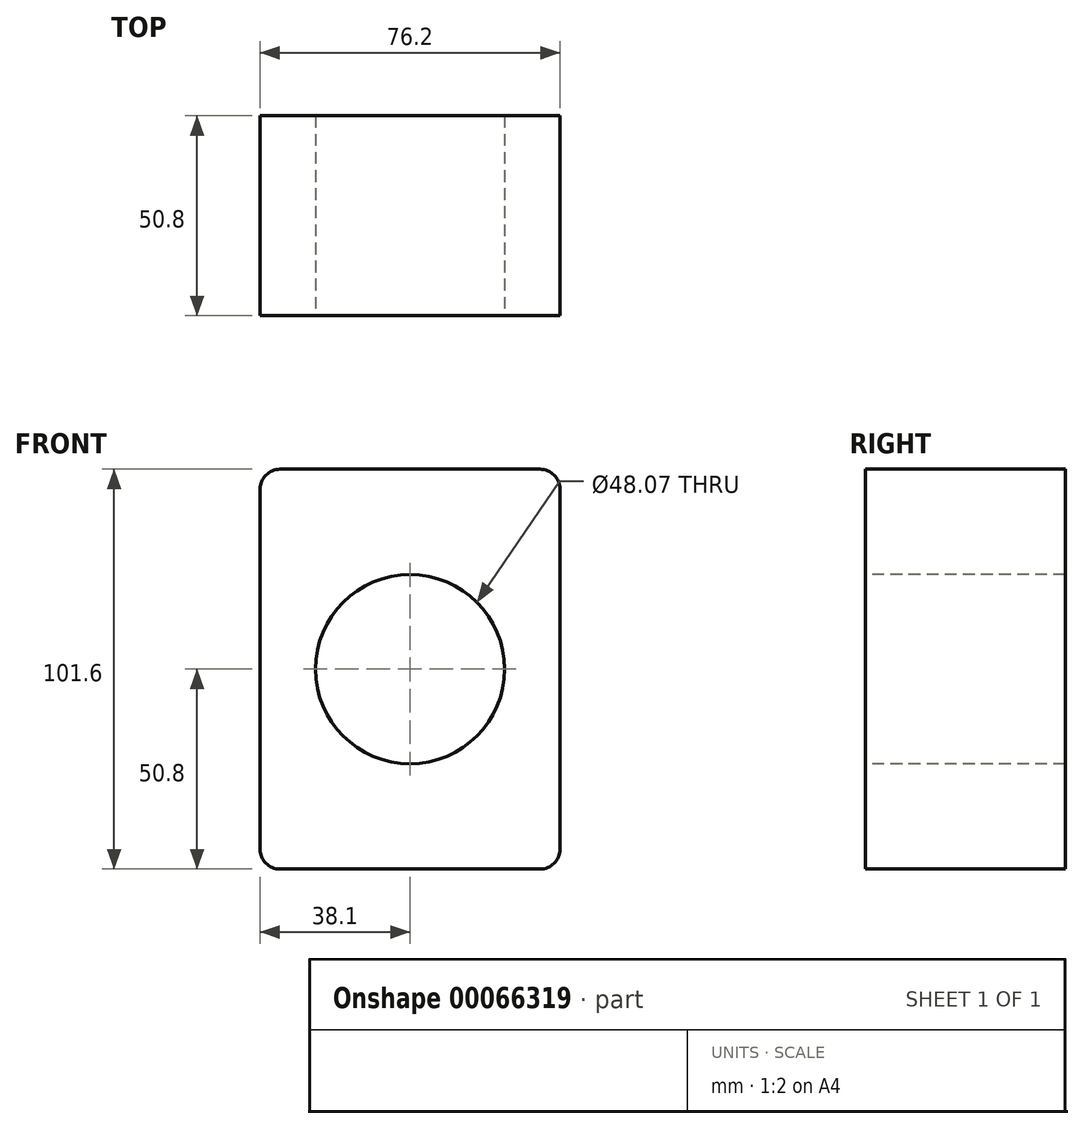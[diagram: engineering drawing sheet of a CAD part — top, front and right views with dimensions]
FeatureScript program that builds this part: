
annotation { "Feature Type Name" : "Feature", "Feature Type Description" : "" }
export const myFeature = defineFeature(function(context is Context, id is Id, definition is map)
    precondition{}
    {
        {
            var Q0;
            Q0=qCreatedBy(makeId("Front.planeOp"),FACE);
            var sketch = newSketch(context, id + "F0", { "sketchPlane" : qUnion([Q0])});
            skLineSegment(sketch, "E0.rect.bottom", {"start": v(38.1, 50.8) * mm, "end": v(-38.1, 50.8) * mm});
            skLineSegment(sketch, "E0.rect.top", {"start": v(38.1, -50.8) * mm, "end": v(-38.1, -50.8) * mm});
            skLineSegment(sketch, "E0.rect.left", {"start": v(38.1, 50.8) * mm, "end": v(38.1, -50.8) * mm});
            skLineSegment(sketch, "E0.rect.right", {"start": v(-38.1, 50.8) * mm, "end": v(-38.1, -50.8) * mm});
            skPoint(sketch, "E0.rect.middle", {"position": v(0, 0) * mm});
            skSolve(sketch);
        }
        {
            var Q0;
            Q0 = qSketchRegion(id + "F0", true);
            extrude(context, id + "F1", {"entities" : qUnion([Q0]), "endBound" : BoundingType.SYMMETRIC, "depth" : 50.8 * mm});
        }
        {
            var Q0;
            Q0=makeQuery(id+"F1.opExtrude","CAP_FACE",FACE,{"disambiguationData":[OSD([sQuery(id+"F0.wireOp",EDGE,"E0.rect.bottom"),sQuery(id+"F0.wireOp",EDGE,"E0.rect.top"),sQuery(id+"F0.wireOp",EDGE,"E0.rect.left"),sQuery(id+"F0.wireOp",EDGE,"E0.rect.right")])],"isStart":false});
            var sketch = newSketch(context, id + "F2", { "sketchPlane" : qUnion([Q0])});
            skCircle(sketch, "E1", {"center": v(0, 0) * mm, "radius": 24.03 * mm});
            skSolve(sketch);
        }
        {
            var Q0;
            Q0 = qSketchRegion(id + "F2", true);
            extrude(context, id + "F3", {"entities" : qUnion([Q0]), "operationType" : NewBodyOperationType.REMOVE, "endBound" : BoundingType.THROUGH_ALL, "oppositeDirection" : true, "depth" : 25.4 * mm});
        }
        {
            var Q0;
            Q0=makeQuery(id+"F1.opExtrude","SWEPT_EDGE",EDGE,{"disambiguationData":[OSD([sQuery(id+"F0.wireOp",EDGE,"E0.rect.bottom"),sQuery(id+"F0.wireOp",EDGE,"E0.rect.right")])]});
            var Q1;
            Q1=makeQuery(id+"F1.opExtrude","SWEPT_EDGE",EDGE,{"disambiguationData":[OSD([sQuery(id+"F0.wireOp",EDGE,"E0.rect.bottom"),sQuery(id+"F0.wireOp",EDGE,"E0.rect.left")])]});
            var Q2;
            Q2=makeQuery(id+"F1.opExtrude","SWEPT_EDGE",EDGE,{"disambiguationData":[OSD([sQuery(id+"F0.wireOp",EDGE,"E0.rect.top"),sQuery(id+"F0.wireOp",EDGE,"E0.rect.left")])]});
            var Q3;
            Q3=makeQuery(id+"F1.opExtrude","SWEPT_EDGE",EDGE,{"disambiguationData":[OSD([sQuery(id+"F0.wireOp",EDGE,"E0.rect.top"),sQuery(id+"F0.wireOp",EDGE,"E0.rect.right")])]});
            fillet(context, id + "F4", {"entities" : qUnion([Q0, Q1, Q2, Q3]), "radius" : 5.08 * mm, "tangentPropagation" : true, "allowEdgeOverflow" : false});
        }
    });
